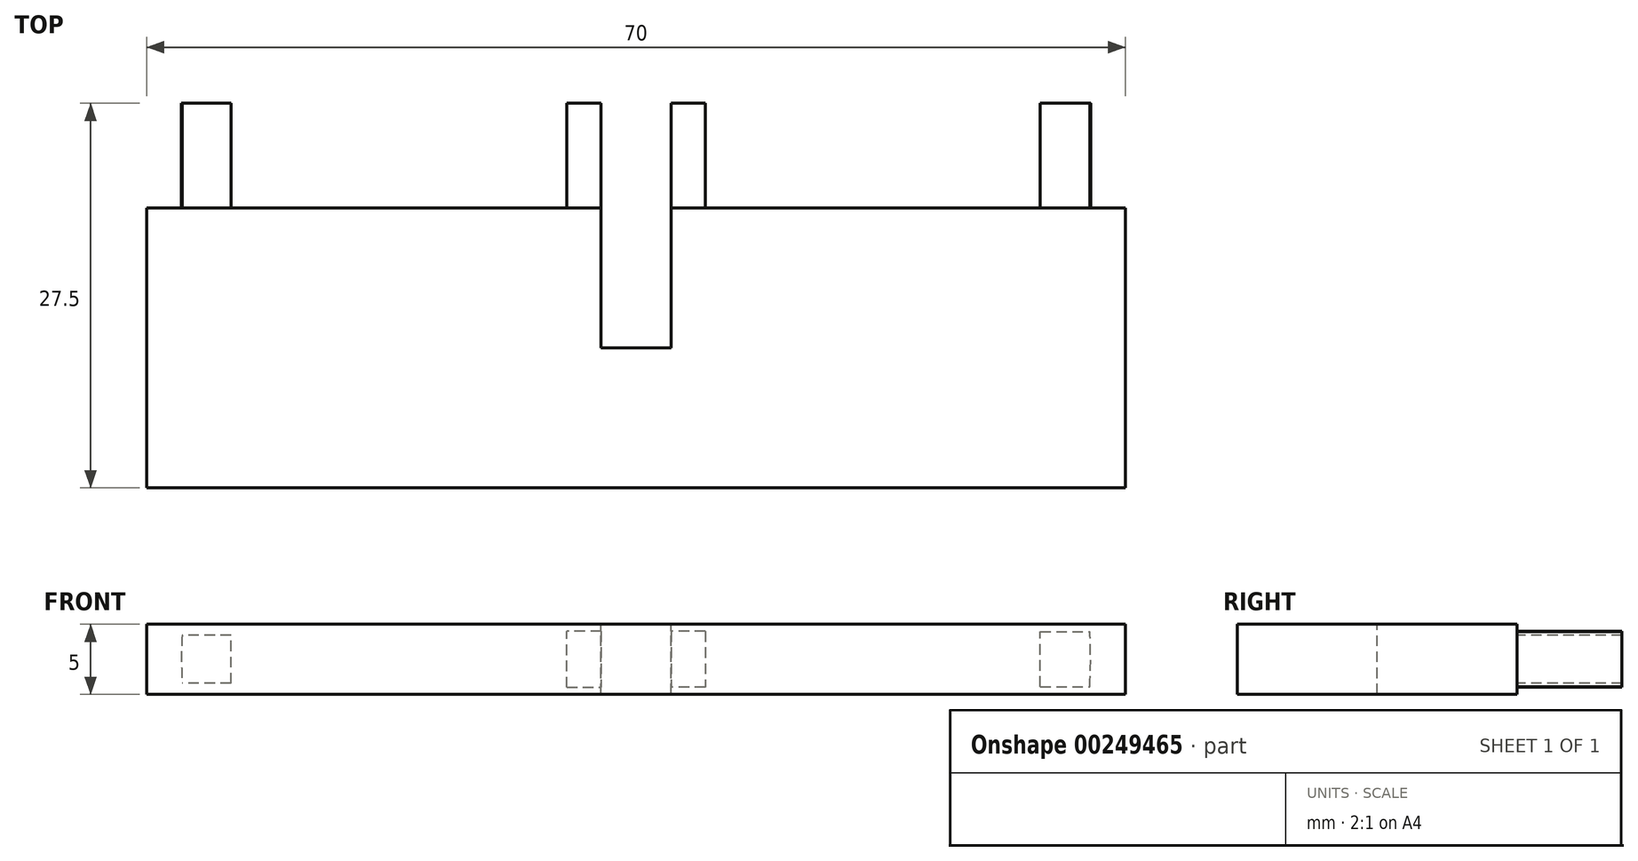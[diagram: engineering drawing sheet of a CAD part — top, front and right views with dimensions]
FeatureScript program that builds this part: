
annotation { "Feature Type Name" : "Feature", "Feature Type Description" : "" }
export const myFeature = defineFeature(function(context is Context, id is Id, definition is map)
    precondition{}
    {
        {
            var Q0;
            Q0=qCreatedBy(makeId("Front.planeOp"),FACE);
            var sketch = newSketch(context, id + "F0", { "sketchPlane" : qUnion([Q0])});
            skLineSegment(sketch, "E0.bottom", {"start": v(-35, -2.5) * mm, "end": v(35, -2.5) * mm});
            skLineSegment(sketch, "E0.top", {"start": v(-35, 2.5) * mm, "end": v(35, 2.5) * mm});
            skLineSegment(sketch, "E0.left", {"start": v(-35, -2.5) * mm, "end": v(-35, 2.5) * mm});
            skLineSegment(sketch, "E0.right", {"start": v(35, -2.5) * mm, "end": v(35, 2.5) * mm});
            skPoint(sketch, "E0.middle", {"position": v(0, 0) * mm});
            skPoint(sketch, "E1", {"position": v(0, 2.5) * mm});
            skSolve(sketch);
        }
        {
            var Q0;
            Q0 = qSketchRegion(id + "F0", true);
            extrude(context, id + "F1", {"entities" : qUnion([Q0]), "depth" : 20 * mm});
        }
        {
            var Q0;
            Q0=qCreatedBy(makeId("Top.planeOp"),FACE);
            var sketch = newSketch(context, id + "F2", { "sketchPlane" : qUnion([Q0])});
            skLineSegment(sketch, "E2", {"start": v(0, 0) * mm, "end": v(-2.5, 0) * mm});
            skLineSegment(sketch, "E3", {"start": v(-2.5, 0) * mm, "end": v(2.5, 0) * mm});
            skLineSegment(sketch, "E4", {"start": v(2.5, 0) * mm, "end": v(2.5, -10) * mm});
            skLineSegment(sketch, "E5", {"start": v(2.5, -10) * mm, "end": v(-2.5, -10) * mm});
            skLineSegment(sketch, "E6", {"start": v(-2.5, -10) * mm, "end": v(-2.5, 0) * mm});
            skLineSegment(sketch, "E7", {"start": v(0, 0) * mm, "end": v(2.5, 0) * mm});
            skSolve(sketch);
        }
        {
            var Q0;
            Q0 = qSketchRegion(id + "F2", true);
            extrude(context, id + "F3", {"entities" : qUnion([Q0]), "operationType" : NewBodyOperationType.REMOVE, "endBound" : BoundingType.THROUGH_ALL, "oppositeDirection" : true, "depth" : 25 * mm});
        }
        {
            var Q0;
            Q0 = qSketchRegion(id + "F2", true);
            extrude(context, id + "F4", {"entities" : qUnion([Q0]), "operationType" : NewBodyOperationType.REMOVE, "endBound" : BoundingType.THROUGH_ALL, "depth" : 25 * mm});
        }
        {
            var Q0;
            Q0=qCreatedBy(makeId("Front.planeOp"),FACE);
            var sketch = newSketch(context, id + "F5", { "sketchPlane" : qUnion([Q0])});
            skArc(sketch, "E8", {"start": v(32.44, -1.96) * mm, "mid": v(32.5, 0) * mm, "end": v(32.44, 1.96) * mm});
            skArc(sketch, "E9.trimOffspring", {"start": v(-32.45, 1.72) * mm, "mid": v(-32.5, 0) * mm, "end": v(-32.45, -1.72) * mm});
            skPoint(sketch, "E10.left.start.orphan", {"position": v(-6.25, -2.5) * mm});
            skPoint(sketch, "E11.orphan", {"position": v(-6.25, 2.5) * mm});
            skPoint(sketch, "E10.right.end.orphan", {"position": v(6.25, 2.5) * mm});
            skPoint(sketch, "E10.right.start.orphan", {"position": v(6.25, -2.5) * mm});
            skLineSegment(sketch, "E12", {"start": v(-4.95, -2) * mm, "end": v(-2.5, -2) * mm});
            skLineSegment(sketch, "E13", {"start": v(-4.95, -2) * mm, "end": v(-4.95, 2) * mm});
            skLineSegment(sketch, "E14", {"start": v(-2.5, 2) * mm, "end": v(-2.5, -2) * mm});
            skLineSegment(sketch, "E15", {"start": v(-2.5, 2) * mm, "end": v(-4.95, 2) * mm});
            skLineSegment(sketch, "E16", {"start": v(4.95, -2) * mm, "end": v(2.5, -2) * mm});
            skLineSegment(sketch, "E17", {"start": v(4.95, 2) * mm, "end": v(2.5, 2) * mm});
            skLineSegment(sketch, "E18", {"start": v(2.5, 2) * mm, "end": v(2.5, -2) * mm});
            skLineSegment(sketch, "E19", {"start": v(4.95, 2) * mm, "end": v(4.95, -2) * mm});
            skLineSegment(sketch, "E20", {"start": v(28.9, 1.96) * mm, "end": v(32.44, 1.96) * mm});
            skLineSegment(sketch, "E21", {"start": v(28.9, -1.96) * mm, "end": v(28.9, 1.96) * mm});
            skLineSegment(sketch, "E22", {"start": v(28.9, -1.96) * mm, "end": v(32.44, -1.96) * mm});
            skLineSegment(sketch, "E23", {"start": v(-28.96, 1.72) * mm, "end": v(-32.45, 1.72) * mm});
            skLineSegment(sketch, "E24", {"start": v(-28.96, -1.72) * mm, "end": v(-32.45, -1.72) * mm});
            skLineSegment(sketch, "E25", {"start": v(-28.96, -1.72) * mm, "end": v(-28.96, 1.72) * mm});
            skSolve(sketch);
        }
        {
            var Q0;
            Q0 = qSketchRegion(id + "F5", true);
            extrude(context, id + "F6", {"entities" : qUnion([Q0]), "operationType" : NewBodyOperationType.ADD, "oppositeDirection" : true, "depth" : 7.5 * mm});
        }
    });
